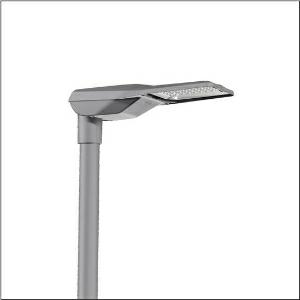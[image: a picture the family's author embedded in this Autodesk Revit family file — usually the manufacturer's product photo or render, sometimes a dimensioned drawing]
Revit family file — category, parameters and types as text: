
# Revit family: streetlight_sl_21_iq_mini___stw1_0a_5xe2e31d08gb_aef3
name_source: partatom
category: Lighting Fixtures
units: mm (PartAtom-declared; Revit-internal decimal feet)

## family parameters
Cut with Voids When Loaded = No
Host = Face
Light Source = No
Part Type = Normal
Room Calculation Point = No
Round Connector Dimension = Use Diameter
Shared = No

## types (1)
- --- (1 x LED, 5680 lm, 37.1 W, 3000K)
    Apparent Load = 37 VA
    CIE Flux Codes = 38 75 98 100 100
    Color Rendering = 70
    Color Temperature = 3000K
    Default Elevation = 1800 mm
    Description = Streetlight SL 21 iQ mini, mast luminaire, primary light control with lens, of PMMA, primary optical cover: cover, of toughened safety glass, transparent, light distribution: STW1.0a, light emission: direct distribution, primary light characteristic: asymmetric, installation type: post-top, side-entry, LED, High Power LED, rated luminous flux: 5.680lm, luminous efficacy: 153lm/W, light colour: 730, colour temperature: 3000K, control gear: iQ-Comfort, control: Auto-Match, Temp-Guard, Lumen-Switch, Night-Set, Smart-Wire, Light-Fading, Desk-Remote (wireless, voltage-free reading and setting of iQ features in the workshop via application-optimized NFC function/RFID function), optimised constant luminous flux control (CLO 2.0), pre-setting: linear dimming characteristic, mains connection: 220..240V, AC, 50/60Hz, start of lifetime: 37W, end of service life: 39W, reduction: 18W, luminaire housing, of diecast aluminium, powder-coated, SITECO metallic grey (DB 702S), corrosivity category C5 high according to DIN EN ISO 12944, please order mast flange separately, inclination adjustable: 0°, 5°, 10°, 15°, sealing non-destructively replaceable, multi-level sealing system, length: 628mm, width: 235mm, height: 110mm, mast flange for spigot size: 42mm (side-entry): 5XC10008XM4, 60/48mm (side-entry/post-top): 5XC10108XM2, 76/60mm (side-entry/post-top): 5XC10108XM1, mounting height: 4..8m, protection rating (complete): IP66, insulation class (complete): insulation class II (safety insulation), certification: CE, ENEC, ENEC+, VDE, impact resistance: IK10, permissible operating ambient temperature for outdoor applications: -40..+50°C, standard-compliant lighting for roads and squares, packaging unit: 1 piece

Light Distribution: STW1.0a
    Height = 110 mm
    Lamp = 1 x LED
    Lamp Light Flux = 5680 lm
    Lamp Power = 37.1 W
    Lamp count = 1
    Length = 625 mm
    Luminous efficacy = 153 lm/W
    Manufacturer = Siteco
    ModVariant = No
    Model = 5XE2E31D08GB
    Number of Poles = 1
    OnlyDefault = Yes
    Power Factor = 1
    Product Name = Streetlight SL 21 iQ mini | STW1.0a
    Product group = mast luminaire | pylon top
    ProductGroupID = 6100
    Protection Class = Protection class II
    Protection Degree = IP 66
    RLX_Detail_Level = 1
    RLX_Emergency_Light_Flux = 0 lm
    RLX_Emergency_Type = 0
    RLX_Emergency_Type_DB = No
    RlxData = <blob elided: 26417 chars, md5=c0af06ac>
    Socket = socket
    Standby Power = 0 W
    System Light Flux = 5680 lm
    System Power = 37 W
    Type Comments = factory setting: luminous flux: 100 % | dim-lin: 254 | 385 mA
    Type Image = l_1003519.jpg
    URL = http://relux.com
    VarID = @adj_185061
    Voltage = 0 V
    Weight = 0.00 kg
    Width = 234 mm

## geometry (parser evidence)
native form markers: Blend x4, Sweep x10
no freeform markers — native parametric forms only
